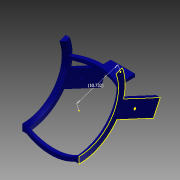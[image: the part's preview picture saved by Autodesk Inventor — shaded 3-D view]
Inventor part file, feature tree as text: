
AUTODESK INVENTOR PART (.ipt)
format: ipt  version: 2014 (Build 180170000, 170)  size: 217,088 bytes
history: native  units: in
note: dims shown in document units (in); Inventor stores cm internally (conversion verified against a paired STEP export)
features: sketch x9, revolve x3, hole x3, extrude x3, plane x2, projected_geometry x2
ambient origin geometry x8: Origin, YZ Plane, XZ Plane, XY Plane, X Axis, Y Axis, Z Axis, Center Point
bodies: Solid1 (feature_tree)
feature tree (22):
  revolve  "Revolution1"  [1 undecoded]
  revolve  "Revolution2"  [1 undecoded]
  plane  "Work Plane1"
  plane  "Work Plane2"
  revolve  "Revolution4"  [1 undecoded]
  sketch  "Sketch9"  dims[d10=12.0in d44=12.0in]
  hole  "Hole3"  [1 undecoded]
  hole  "Hole4"  [1 undecoded]
  extrude  "Extrusion3"  Depth=1.0in
  extrude  "Extrusion4"  Depth=0.72in
  hole  "Hole5"  [1 undecoded]
  extrude  "Extrusion5"  Depth=1.0in TaperAngle=0.0deg
  sketch  "Sketch14"  dims[d66=0.1718in d67=10.0in d68=0.1718in d69=1.0in d70=0.0in d71=1.0in d72=0.0in d73=6.0in d74=0.5in d75=0.75in d76=0.375in d77=0.25in d78=0.5635in d79=1.0in d80=0.8108in d81=3.5in d82=3.0in d83=0.72in d84=0.0in d85=3.0in d86=10.7316in]
  sketch  "Sketch1"  dims[d1=12.0in d3=12.0in]
  sketch  "Sketch2"  dims[d5=0.7559in d6=12.0in]
  projected_geometry  "Projected Loop1"
  sketch  "Sketch8"  dims[d7=12.0in d9=0.0275in]
  sketch  "Sketch10"  dims[d45=12.0in d46=0.0275in]
  sketch  "Sketch11"  dims[d47=0.5in]
  sketch  "Sketch12"  dims[d48=0.25in d49=0.75in d50=0.375in d51=0.25in d52=0.5635in d53=1.0in d54=0.8108in]
  sketch  "Sketch13"  dims[d55=0.25in d56=0.75in d57=0.375in d58=0.25in d59=0.5635in d60=1.0in d61=0.8108in d65=10.0in]
  projected_geometry  "Project Cut Edges2"
note: 6 required parameter values undecoded (feature->parameter linkage not recoverable at this tier; creation-order binding heuristic only, values carry confidence <= 0.55)